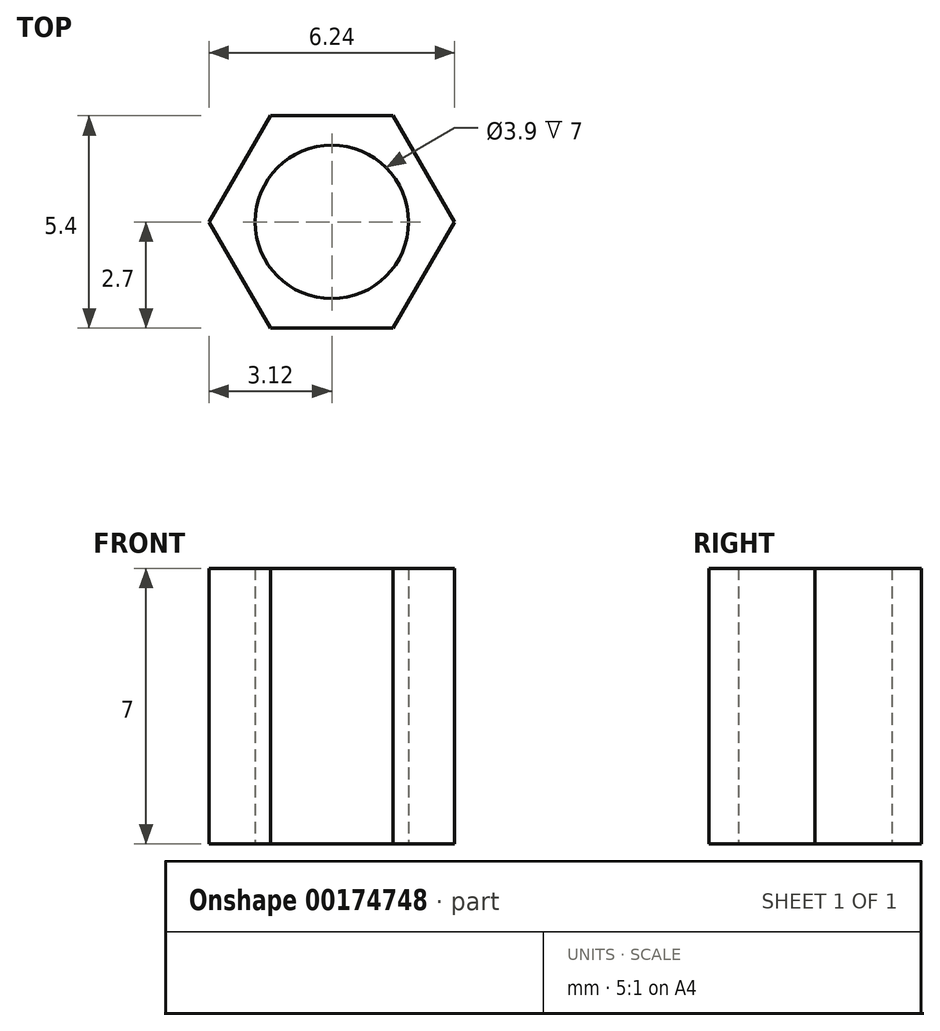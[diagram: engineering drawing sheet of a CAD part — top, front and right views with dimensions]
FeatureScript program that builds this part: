
annotation { "Feature Type Name" : "Feature", "Feature Type Description" : "" }
export const myFeature = defineFeature(function(context is Context, id is Id, definition is map)
    precondition{}
    {
        {
            var Q0;
            Q0=qCreatedBy(makeId("Top.planeOp"),FACE);
            var sketch = newSketch(context, id + "F0", { "sketchPlane" : qUnion([Q0])});
            skCircle(sketch, "E0.cCircle", {"center": v(0, 0) * mm, "radius": 2.7 * mm, "construction": true});
            skLineSegment(sketch, "E0.0", {"start": v(-1.56, 2.7) * mm, "end": v(1.56, 2.7) * mm});
            skLineSegment(sketch, "E0.1", {"start": v(1.56, 2.7) * mm, "end": v(3.12, 0) * mm});
            skLineSegment(sketch, "E0.2", {"start": v(3.12, 0) * mm, "end": v(1.56, -2.7) * mm});
            skLineSegment(sketch, "E0.3", {"start": v(1.56, -2.7) * mm, "end": v(-1.56, -2.7) * mm});
            skLineSegment(sketch, "E0.4", {"start": v(-1.56, -2.7) * mm, "end": v(-3.12, 0) * mm});
            skLineSegment(sketch, "E0.5", {"start": v(-3.12, 0) * mm, "end": v(-1.56, 2.7) * mm});
            skPoint(sketch, "E0.0.midPoint", {"position": v(0, 2.7) * mm});
            skCircle(sketch, "E1", {"center": v(0, 0) * mm, "radius": 1.95 * mm});
            skSolve(sketch);
        }
        {
            var Q0;
            Q0 = qSketchRegion(id + "F0", true);
            extrude(context, id + "F1", {"entities" : qUnion([Q0]), "offsetDistance" : 25 * mm, "depth" : 7 * mm});
        }
    });
